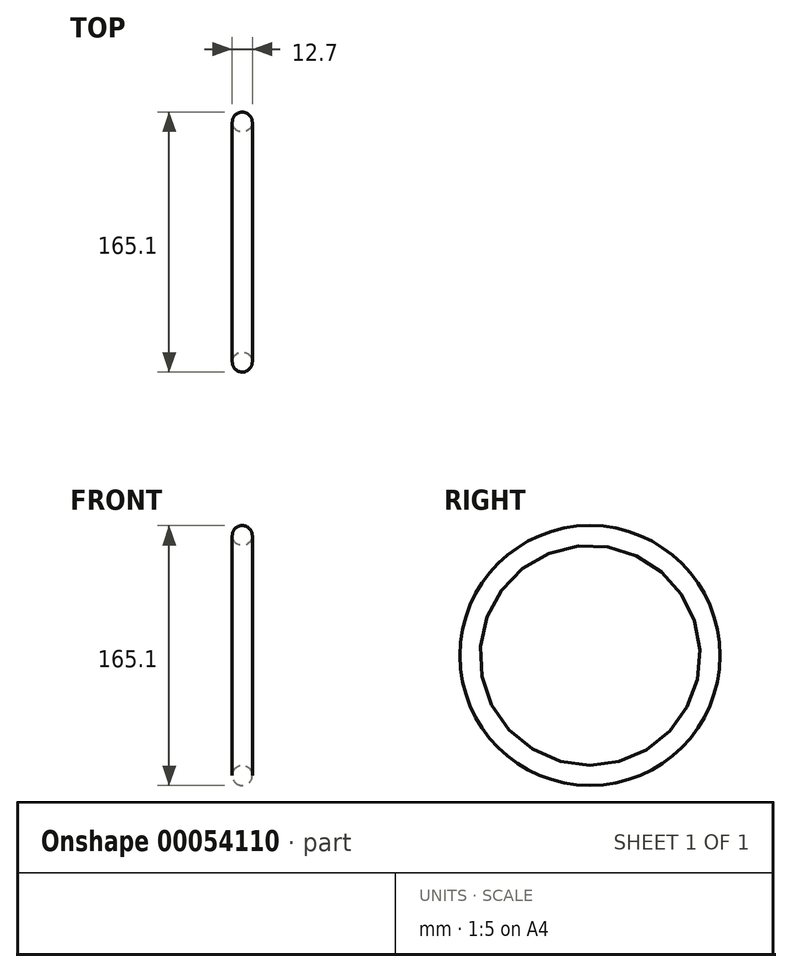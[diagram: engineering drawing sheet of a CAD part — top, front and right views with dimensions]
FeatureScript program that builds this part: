
annotation { "Feature Type Name" : "Feature", "Feature Type Description" : "" }
export const myFeature = defineFeature(function(context is Context, id is Id, definition is map)
    precondition{}
    {
        {
            var Q0;
            Q0=qCreatedBy(makeId("Front.planeOp"),FACE);
            var sketch = newSketch(context, id + "F0", { "sketchPlane" : qUnion([Q0])});
            skCircle(sketch, "E0", {"center": v(0, 76.2) * mm, "radius": 6.35 * mm});
            skSolve(sketch);
        }
        {
            var Q0;
            Q0=qCreatedBy(makeId("Right.planeOp"),FACE);
            var sketch = newSketch(context, id + "F1", { "sketchPlane" : qUnion([Q0])});
            skCircle(sketch, "E1", {"center": v(0, 0) * mm, "radius": 76.2 * mm});
            skSolve(sketch);
        }
        {
            var Q0;
            Q0=makeQuery(id+"F0.imprint","IMPRINT",FACE,{"disambiguationData":[TD([[makeQuery(id+"F0.imprint","IMPRINT",EDGE,{"derivedFrom":sQuery(id+"F0.wireOp",EDGE,"E0")}),1.0]])]});
            var Q1;
            Q1=sQuery(id+"F1.wireOp",EDGE,"E1");
            sweep(context, id + "F2", {"profiles" : qUnion([Q0]), "path" : qUnion([Q1])});
        }
    });
